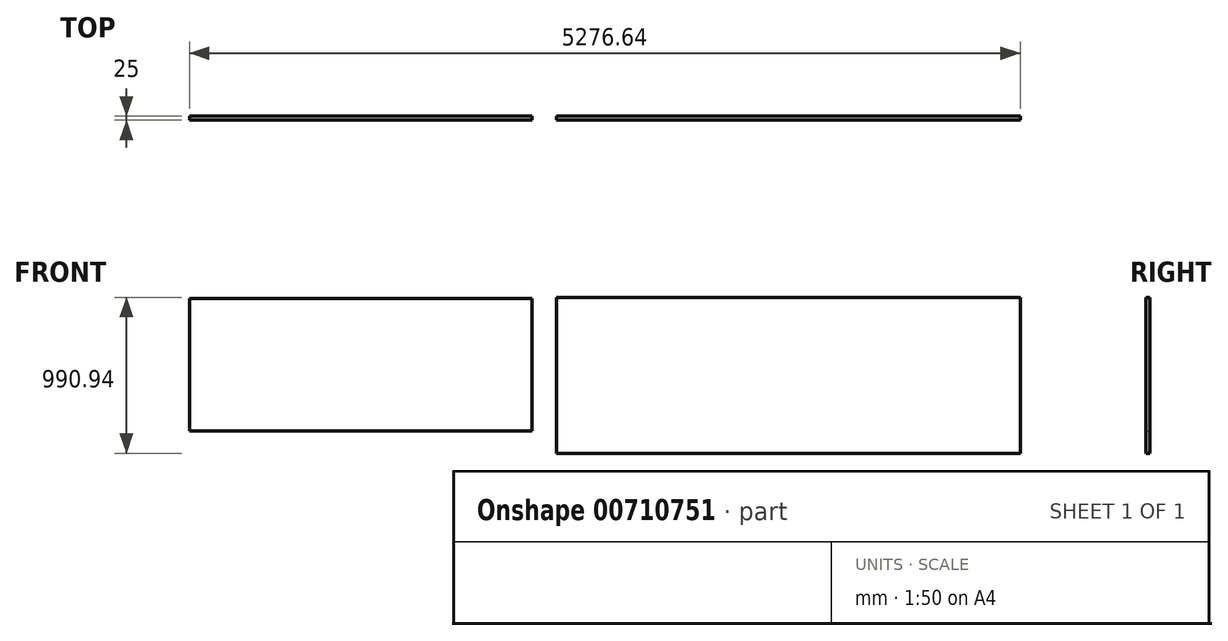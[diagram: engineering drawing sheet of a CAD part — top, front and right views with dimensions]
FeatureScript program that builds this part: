
annotation { "Feature Type Name" : "Feature", "Feature Type Description" : "" }
export const myFeature = defineFeature(function(context is Context, id is Id, definition is map)
    precondition{}
    {
        {
            var Q0;
            Q0=qCreatedBy(makeId("Front.planeOp"), FACE);
            var sketch = newSketch(context, id + "F0", { "sketchPlane" : qUnion([Q0])});
            skLineSegment(sketch, "E0.bottom", {"start": v(11586.24, 1928.7) * mm, "end": v(14530.49, 1928.7) * mm});
            skLineSegment(sketch, "E0.top", {"start": v(11586.24, 2919.64) * mm, "end": v(14530.49, 2919.64) * mm});
            skLineSegment(sketch, "E0.left", {"start": v(11586.24, 1928.7) * mm, "end": v(11586.24, 2919.64) * mm});
            skLineSegment(sketch, "E0.right", {"start": v(14530.49, 1928.7) * mm, "end": v(14530.49, 2919.64) * mm});
            skLineSegment(sketch, "E1.bottom", {"start": v(11431.11, 2071.64) * mm, "end": v(9253.85, 2071.64) * mm});
            skLineSegment(sketch, "E1.top", {"start": v(11431.11, 2911.6) * mm, "end": v(9253.85, 2911.6) * mm});
            skLineSegment(sketch, "E1.left", {"start": v(11431.11, 2071.64) * mm, "end": v(11431.11, 2911.6) * mm});
            skLineSegment(sketch, "E1.right", {"start": v(9253.85, 2071.64) * mm, "end": v(9253.85, 2911.6) * mm});
            skSolve(sketch);
        }
        {
            var Q0;
            Q0 = qSketchRegion(id + "F0", true);
            extrude(context, id + "F1", {"entities" : qUnion([Q0]), "depth" : 25 * mm, "offsetDistance" : 25 * mm});
        }
    });
